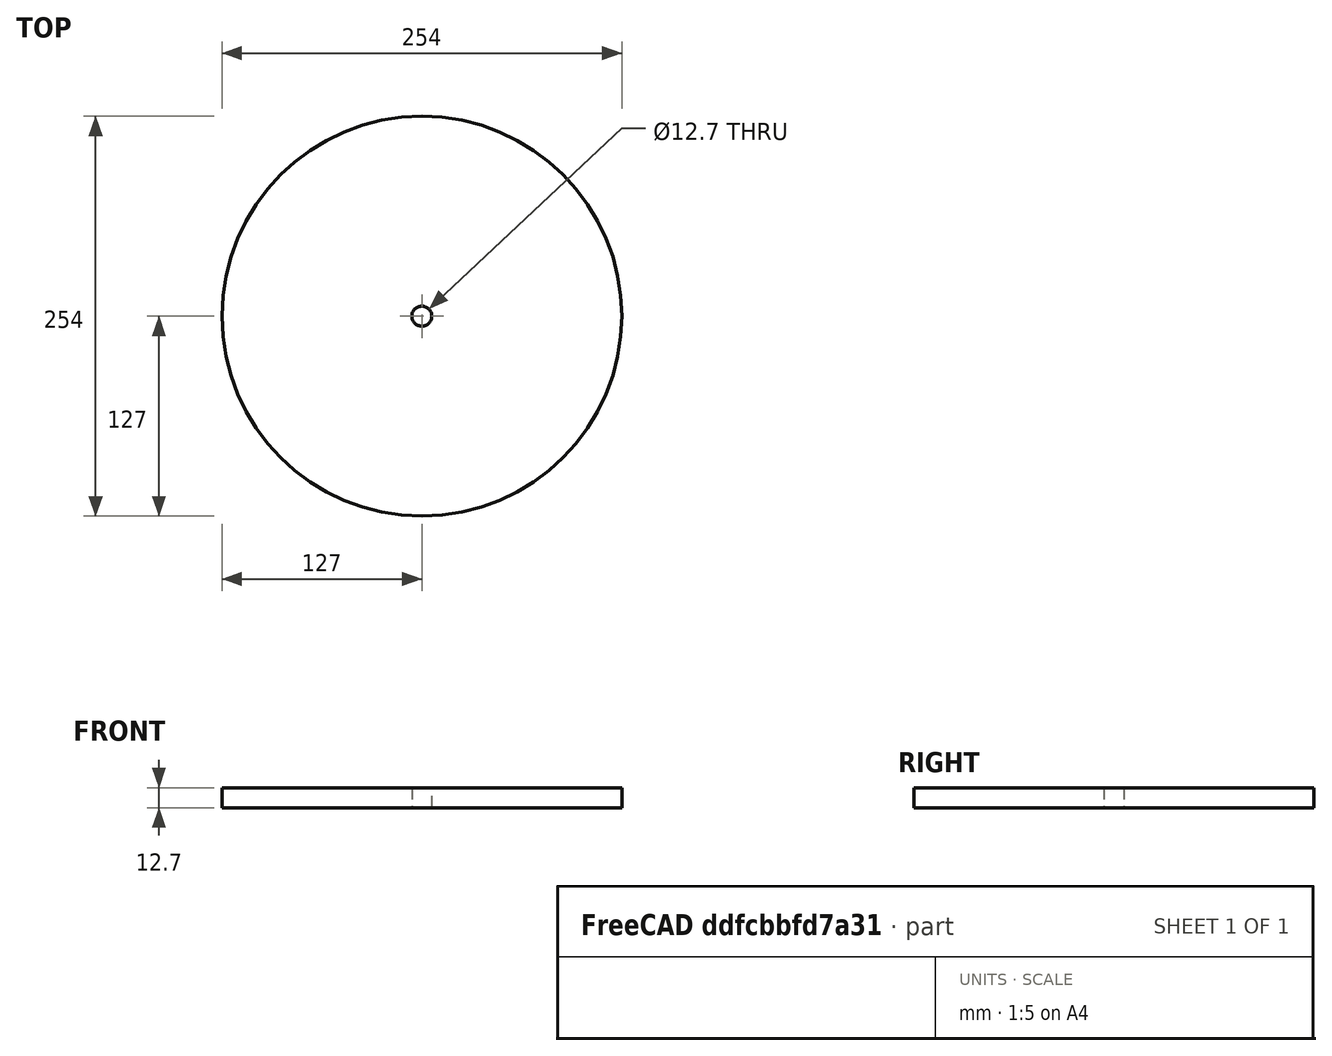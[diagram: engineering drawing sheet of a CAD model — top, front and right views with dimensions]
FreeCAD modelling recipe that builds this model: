
FCSTD DOCUMENT  (FreeCAD 0.19R24291 (Git))
Label: RAdisk
License: All rights reserved
LicenseURL: http://en.wikipedia.org/wiki/All_rights_reserved
objects: TechDraw::DrawViewDimension×2, Sketcher::SketchObject×1, PartDesign::Pad×1, PartDesign::Body×1, TechDraw::DrawSVGTemplate×1, TechDraw::DrawProjGroupItem×1, TechDraw::DrawProjGroup×1, TechDraw::DrawPage×1
note: 4 computed .brp shape members not serialized (recipe doc carries the construction recipe); baked Part::Feature solids carry a one-line shape summary decoded from their .brp

FEATURE [Sketcher::SketchObject] Sketch
  FullyConstrained = true
  MapMode = 5
  Support = -> [XY_Plane]
  sketch-geometry (2):
    g0: Circle CenterX=0 CenterY=0 CenterZ=0 NormalX=0 NormalY=0 NormalZ=1 AngleXU=0 Radius=6.35
    g1: Circle CenterX=0 CenterY=0 CenterZ=0 NormalX=0 NormalY=0 NormalZ=1 AngleXU=0 Radius=127
  constraints (4):
    c: Coincident(g0,g-1)
    c: Coincident(g1,g0)
    c: Diameter(g0) = 12.7
    c: Diameter(g1) = 254
FEATURE [PartDesign::Pad] Pad
  Direction = (1,1,1)
  Length = 12.7
  Length2 = 100
  Profile = -> Sketch
  Type = 0
FEATURE [PartDesign::Body] Body  label="BodyRAdisk"
  Group = -> [Sketch,Pad]
  Origin = -> Origin
  Tip = -> Pad
FEATURE [TechDraw::DrawSVGTemplate] Template
  EditableTexts = Approved1=Approved 1; Approved2=Approved 2; CheckedBy=Checked By; Code=Code; CompanyAddress=https://github.com/<owner>/PST_Mount; CompanyName=Amused Scientist; DrawingNumber=Drawing Number; DrawingTitle1=Drawing Title 1; DrawingTitle2=Drawing Title 2; DrawingTitle3=Drawing Title 3; DrawnBy=Drawn By; Revision=Rev; Scale=Scale; Sheet=Sheet n of m
  Height = 215.9
  Orientation = 1
  Width = 279.4
FEATURE [TechDraw::DrawProjGroupItem] ProjItem  label="Front"
  CoarseView = false
  Direction = (0,0,1)
  Focus = 100
  HardHidden = false
  IsoCount = 0
  IsoHidden = false
  IsoVisible = false
  LockPosition = true
  Perspective = false
  Rotation = 0
  RotationVector = (1,0,0)
  Scale = 0.5
  ScaleType = 2
  SeamHidden = false
  SeamVisible = true
  SmoothHidden = false
  SmoothVisible = true
  Source = -> [Body]
  Type = 0
  X = 0
  XDirection = (1,0,0)
  Y = 0
FEATURE [TechDraw::DrawProjGroup] ProjGroup
  Anchor = -> ProjItem
  AutoDistribute = true
  LockPosition = false
  ProjectionType = 0
  Rotation = 0
  Scale = 0.5
  ScaleType = 2
  Source = -> [Body]
  Views = -> [ProjItem]
  X = 94.9828
  Y = 128.911
  spacingX = 15
  spacingY = 15
FEATURE [TechDraw::DrawViewDimension] Dimension002
  Arbitrary = false
  ArbitraryTolerances = false
  EqualTolerance = true
  FormatSpec = ⌀%.3f
  FormatSpecOverTolerance = %+.3f
  FormatSpecUnderTolerance = %+.3f
  Inverted = false
  LockPosition = false
  MeasureType = 1
  OverTolerance = 0
  References2D = -> [ProjItem]
  Rotation = 0
  ScaleType = 2
  TheoreticalExact = false
  Type = 5
  UnderTolerance = 0
  X = 76.5665
  Y = 39.0111
FEATURE [TechDraw::DrawViewDimension] Dimension
  Arbitrary = false
  ArbitraryTolerances = false
  EqualTolerance = true
  FormatSpec = ⌀%.3f
  FormatSpecOverTolerance = %+.3f
  FormatSpecUnderTolerance = %+.3f
  Inverted = false
  LockPosition = false
  MeasureType = 1
  OverTolerance = 0
  References2D = -> [ProjItem]
  Rotation = 0
  ScaleType = 2
  TheoreticalExact = false
  Type = 5
  UnderTolerance = 0
  X = 9.31607
  Y = 24.4547
FEATURE [TechDraw::DrawPage] Page
  KeepUpdated = true
  NextBalloonIndex = 1
  ProjectionType = 0
  Template = -> Template
  Views = -> [ProjGroup,Dimension002,Dimension]
